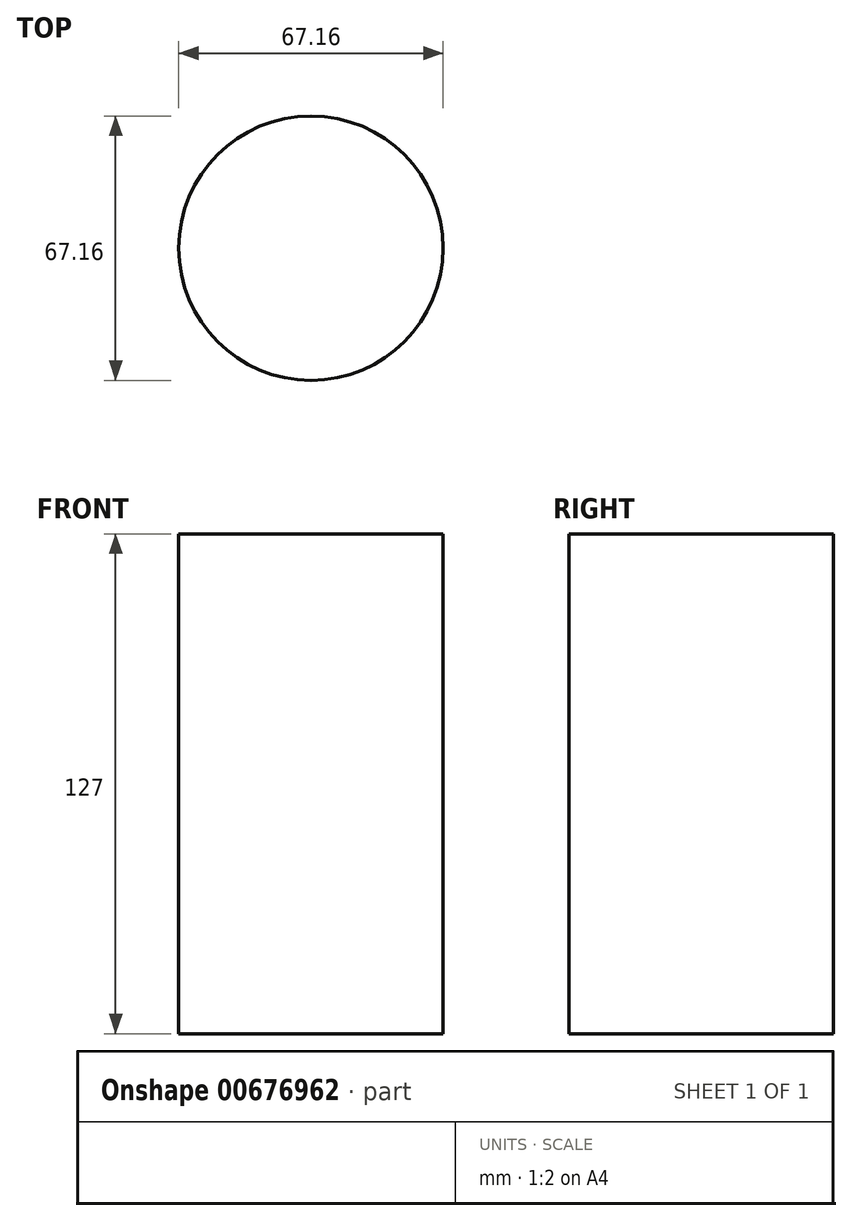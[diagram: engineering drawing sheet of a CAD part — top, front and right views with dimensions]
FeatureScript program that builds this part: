
annotation { "Feature Type Name" : "Feature", "Feature Type Description" : "" }
export const myFeature = defineFeature(function(context is Context, id is Id, definition is map)
    precondition{}
    {
        {
            var Q0;
            Q0=qCreatedBy(makeId("Top.planeOp"),FACE);
            var sketch = newSketch(context, id + "F0", { "sketchPlane" : qUnion([Q0])});
            skCircle(sketch, "E0", {"center": v(0, 0) * mm, "radius": 33.58 * mm});
            skSolve(sketch);
        }
        {
            var Q0;
            Q0=makeQuery(id+"F0.imprint","IMPRINT",FACE,{"disambiguationData":[TD([[makeQuery(id+"F0.imprint","IMPRINT",EDGE,{"derivedFrom":sQuery(id+"F0.wireOp",EDGE,"E0")}),1.0]])]});
            extrude(context, id + "F1", {"entities" : qUnion([Q0]), "depth" : 127 * mm, "offsetDistance" : 25.4 * mm});
        }
    });
